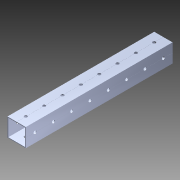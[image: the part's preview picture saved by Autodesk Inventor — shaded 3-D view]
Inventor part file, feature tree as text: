
AUTODESK INVENTOR PART (.ipt)
format: ipt  version: 2014 (Build 180170000, 170)  size: 1,219,072 bytes
history: native  units: in
note: dims shown in document units (in); Inventor stores cm internally (conversion verified against a paired STEP export)
features: extrude x2, sketch x2, pattern_circular x1, other x1, imported_body x1
ambient origin geometry x8: Origin, YZ Plane, XZ Plane, XY Plane, X Axis, Y Axis, Z Axis, Center Point
bodies: Body1 (feature_tree)
feature tree (7):
  pattern_circular  "CirPattern2"
  other  "1x1 tube1"
  extrude  "Extrusion1"  Depth=1.0in TaperAngle=0.0deg
  extrude  "Extrusion2"  [1 undecoded]
  imported_body  "Base1"
  sketch  "Sketch1"  dims[d0=50.0in d1=0.0in d2=1.0in d3=0.0in]
  sketch  "Sketch3"
note: 1 required parameter value undecoded (feature->parameter linkage not recoverable at this tier; creation-order binding heuristic only, values carry confidence <= 0.55)
